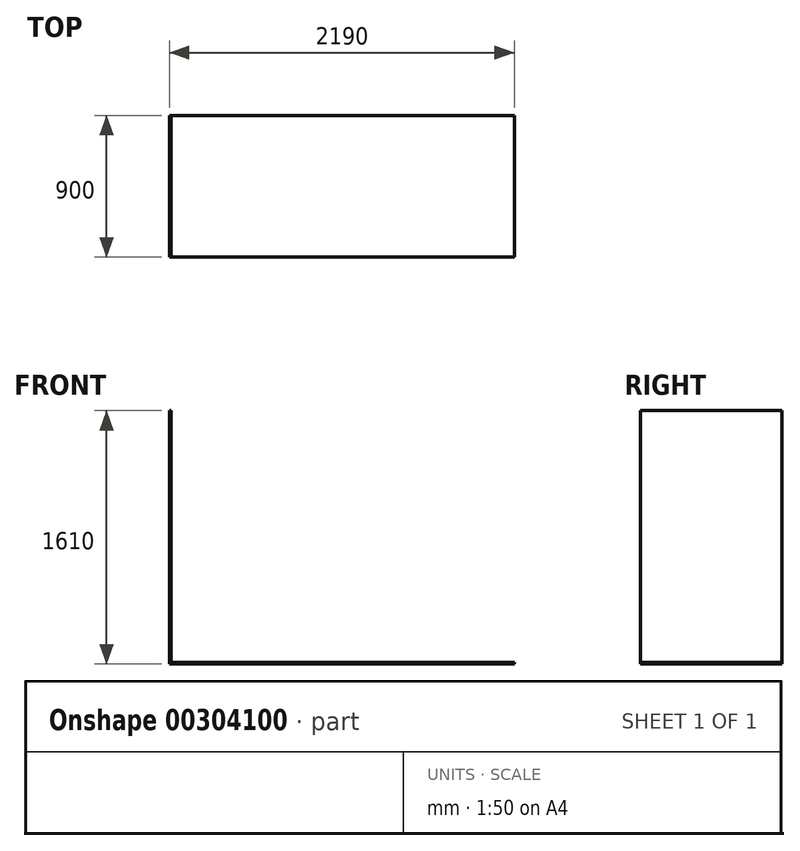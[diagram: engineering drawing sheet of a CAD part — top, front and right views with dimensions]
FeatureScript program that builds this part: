
annotation { "Feature Type Name" : "Feature", "Feature Type Description" : "" }
export const myFeature = defineFeature(function(context is Context, id is Id, definition is map)
    precondition{}
    {
        {
            var Q0;
            Q0=qCreatedBy(makeId("Top.planeOp"),FACE);
            var sketch = newSketch(context, id + "F0", { "sketchPlane" : qUnion([Q0])});
            skLineSegment(sketch, "E0.bottom", {"start": v(-1113.17, -598.25) * mm, "end": v(1076.83, -598.25) * mm});
            skLineSegment(sketch, "E0.top", {"start": v(-1113.17, -1498.25) * mm, "end": v(1076.83, -1498.25) * mm});
            skLineSegment(sketch, "E0.left", {"start": v(-1113.17, -598.25) * mm, "end": v(-1113.17, -1498.25) * mm});
            skLineSegment(sketch, "E0.right", {"start": v(1076.83, -598.25) * mm, "end": v(1076.83, -1498.25) * mm});
            skSolve(sketch);
        }
        {
            var Q0;
            Q0=makeQuery(id+"F0.imprint","IMPRINT",FACE,{"disambiguationData":[TD([[makeQuery(id+"F0.imprint","IMPRINT",EDGE,{"derivedFrom":sQuery(id+"F0.wireOp",EDGE,"E0.bottom")}),-1.0]])]});
            extrude(context, id + "F1", {"entities" : qUnion([Q0]), "depth" : 10 * mm, "offsetDistance" : 25 * mm});
        }
        {
            var Q0;
            Q0=makeQuery(id+"F1.opExtrude","CAP_FACE",FACE,{"disambiguationData":[OSD([sQuery(id+"F0.wireOp",EDGE,"E0.bottom"),sQuery(id+"F0.wireOp",EDGE,"E0.top"),sQuery(id+"F0.wireOp",EDGE,"E0.left"),sQuery(id+"F0.wireOp",EDGE,"E0.right")])],"isStart":false});
            var sketch = newSketch(context, id + "F2", { "sketchPlane" : qUnion([Q0])});
            skLineSegment(sketch, "E1.bottom", {"start": v(-1113.17, -598.25) * mm, "end": v(-1103.17, -598.25) * mm});
            skLineSegment(sketch, "E1.top", {"start": v(-1113.17, -1498.25) * mm, "end": v(-1103.17, -1498.25) * mm});
            skLineSegment(sketch, "E1.left", {"start": v(-1113.17, -598.25) * mm, "end": v(-1113.17, -1498.25) * mm});
            skLineSegment(sketch, "E1.right", {"start": v(-1103.17, -598.25) * mm, "end": v(-1103.17, -1498.25) * mm});
            skSolve(sketch);
        }
        {
            var Q0;
            Q0=makeQuery(id+"F2.imprint","IMPRINT",FACE,{"disambiguationData":[TD([[makeQuery(id+"F2.imprint","IMPRINT",EDGE,{"derivedFrom":sQuery(id+"F2.wireOp",EDGE,"E1.bottom")}),-1.0]])]});
            extrude(context, id + "F3", {"entities" : qUnion([Q0]), "operationType" : NewBodyOperationType.ADD, "depth" : 1600 * mm, "offsetDistance" : 25 * mm});
        }
    });
